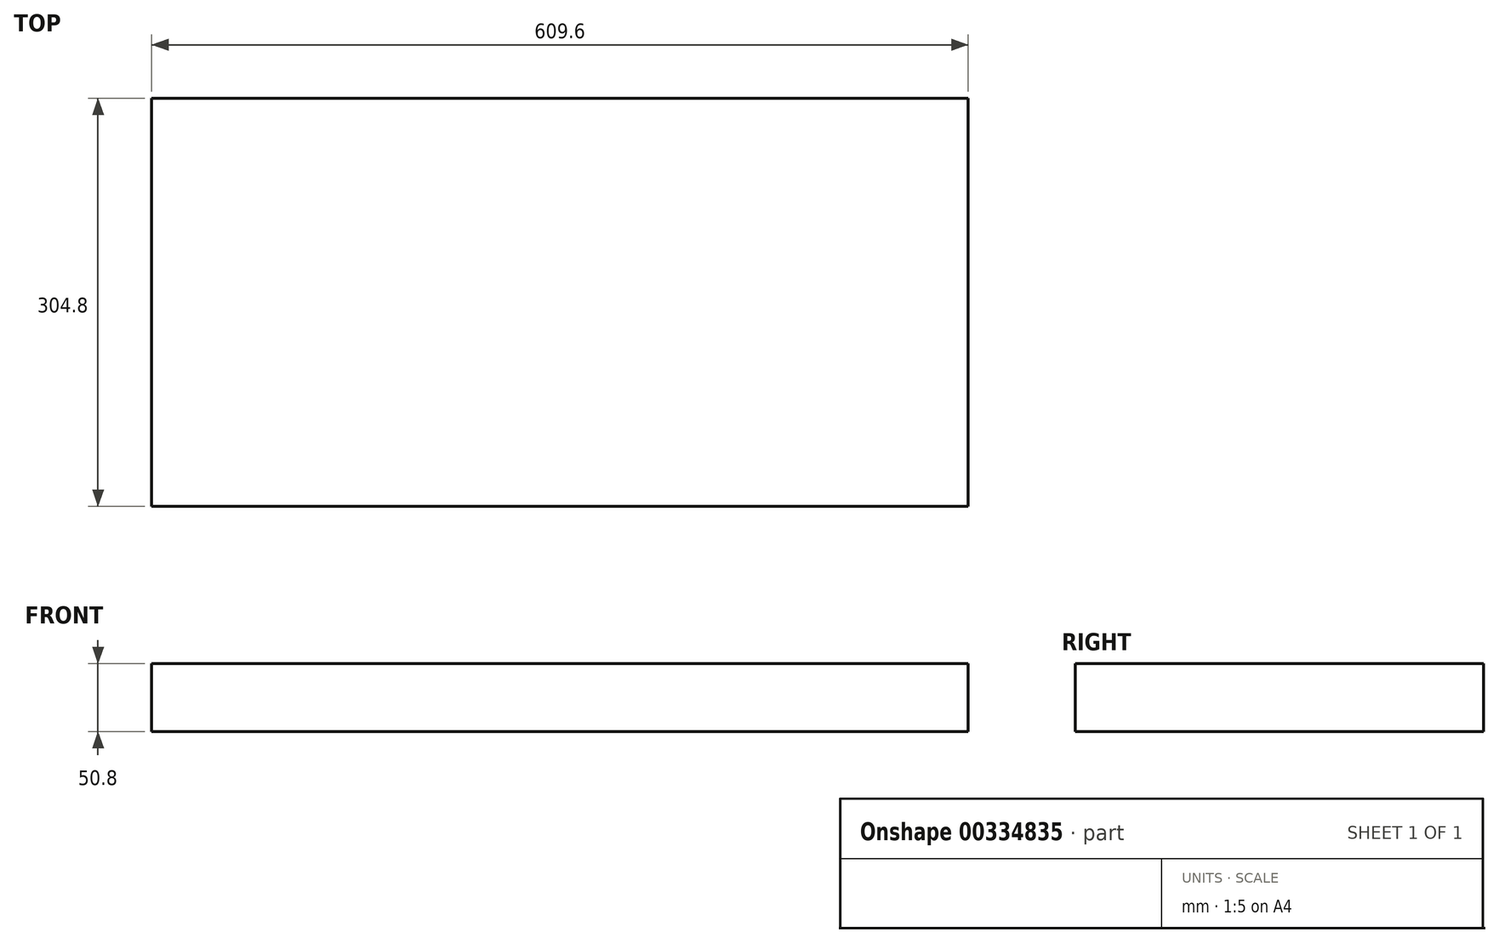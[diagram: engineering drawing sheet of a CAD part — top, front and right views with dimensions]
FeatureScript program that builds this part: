
annotation { "Feature Type Name" : "Feature", "Feature Type Description" : "" }
export const myFeature = defineFeature(function(context is Context, id is Id, definition is map)
    precondition{}
    {
        {
            var Q0;
            Q0=qCreatedBy(makeId("Top.planeOp"),FACE);
            var sketch = newSketch(context, id + "F0", { "sketchPlane" : qUnion([Q0])});
            skLineSegment(sketch, "E0.bottom", {"start": v(-274.37, 203.5) * mm, "end": v(335.23, 203.5) * mm});
            skLineSegment(sketch, "E0.top", {"start": v(-274.37, -101.3) * mm, "end": v(335.23, -101.3) * mm});
            skLineSegment(sketch, "E0.left", {"start": v(-274.37, 203.5) * mm, "end": v(-274.37, -101.3) * mm});
            skLineSegment(sketch, "E0.right", {"start": v(335.23, 203.5) * mm, "end": v(335.23, -101.3) * mm});
            skSolve(sketch);
        }
        {
            var Q0;
            Q0=makeQuery(id+"F0.imprint","IMPRINT",FACE,{"disambiguationData":[TD([[makeQuery(id+"F0.imprint","IMPRINT",EDGE,{"derivedFrom":sQuery(id+"F0.wireOp",EDGE,"E0.bottom")}),-1.0]])]});
            extrude(context, id + "F1", {"entities" : qUnion([Q0]), "depth" : 50.8 * mm});
        }
    });
